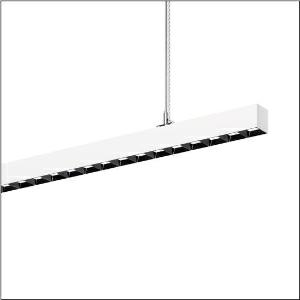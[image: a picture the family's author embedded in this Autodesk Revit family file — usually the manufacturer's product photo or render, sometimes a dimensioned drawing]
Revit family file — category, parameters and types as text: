
# Revit family: silica_r__21_51mx32dc3dwb_4ada
name_source: partatom
category: Lighting Fixtures
units: mm (PartAtom-declared; Revit-internal decimal feet)

## family parameters
Cut with Voids When Loaded = No
Host = Face
Light Source = No
Part Type = Normal
Room Calculation Point = No
Round Connector Dimension = Use Diameter
Shared = No

## types (1)
- --- (1 x LED, 18220 lm, 113 W, 3000K)
    Apparent Load = 113 VA
    CIE Flux Codes = 86 99 100 59 100
    Color Rendering = 80
    Color Temperature = 3000K
    Default Elevation = 1800 mm
    Description = Silica® 21, office luminaire, primary light control with darklight reflector, of PMMA, black, CAT 2 (L<= 3000cd/m²), light emission: direct/indirect distribution, primary light characteristic: symmetric, installation type: suspended mounting, LED, rated luminous flux: 18.220lm, luminous efficacy: 161lm/W, light colour: 830, colour temperature: 3000K, with terminal, 3+2-pole, max. 2.5mm², mains connection: 220..240V, AC, 50/60Hz, rated input power: 113W, luminaire housing, of aluminium, traffic white (RAL 9016), length: 3.004mm, width: 53mm, height: 53mm, protection rating (complete): IP20, insulation class (complete): insulation class I (protective earthing), certification: CE, permissible operating ambient temperature: 0..+35°C, standard: EN 50419, packaging unit: 1 piece
    Height = 53 mm
    Lamp = 1 x LED
    Lamp Light Flux = 18220 lm
    Lamp Power = 113 W
    Lamp count = 1
    Length = 3004 mm
    Luminous efficacy = 161 lm/W
    Manufacturer = Siteco
    ModVariant = No
    Model = 51MX32DC3DWB
    Mounting Place = Ceiling
    Mounting Type = Pendant
    Number of Poles = 1
    OnlyDefault = Yes
    Power Factor = 1
    Product Name = Silica® 21
    Product group = office luminaire | ceiling pendant
    ProductGroupID = 902
    Protection Class = Protection class I
    Protection Degree = IP 20
    RLX_Detail_Level = 1
    RLX_Emergency_Light_Flux = 0 lm
    RLX_Emergency_Type = 0
    RLX_Emergency_Type_DB = No
    RlxData = <blob elided: 64301 chars, md5=c2532b45>
    Socket = socket
    Standby Power = 0 W
    System Light Flux = 18220 lm
    System Power = 113 W
    Type Comments = factory setting: luminous flux: 100 % | dim-lin: 254 | 391 mA
    Type Image = l_1297801.jpg
    URL = http://relux.com
    VarID = @adj_052889
    Voltage = 0 V
    Weight = 0.00 kg
    Width = 53 mm

## geometry (parser evidence)
native form markers: Blend x4, Sweep x11
no freeform markers — native parametric forms only
